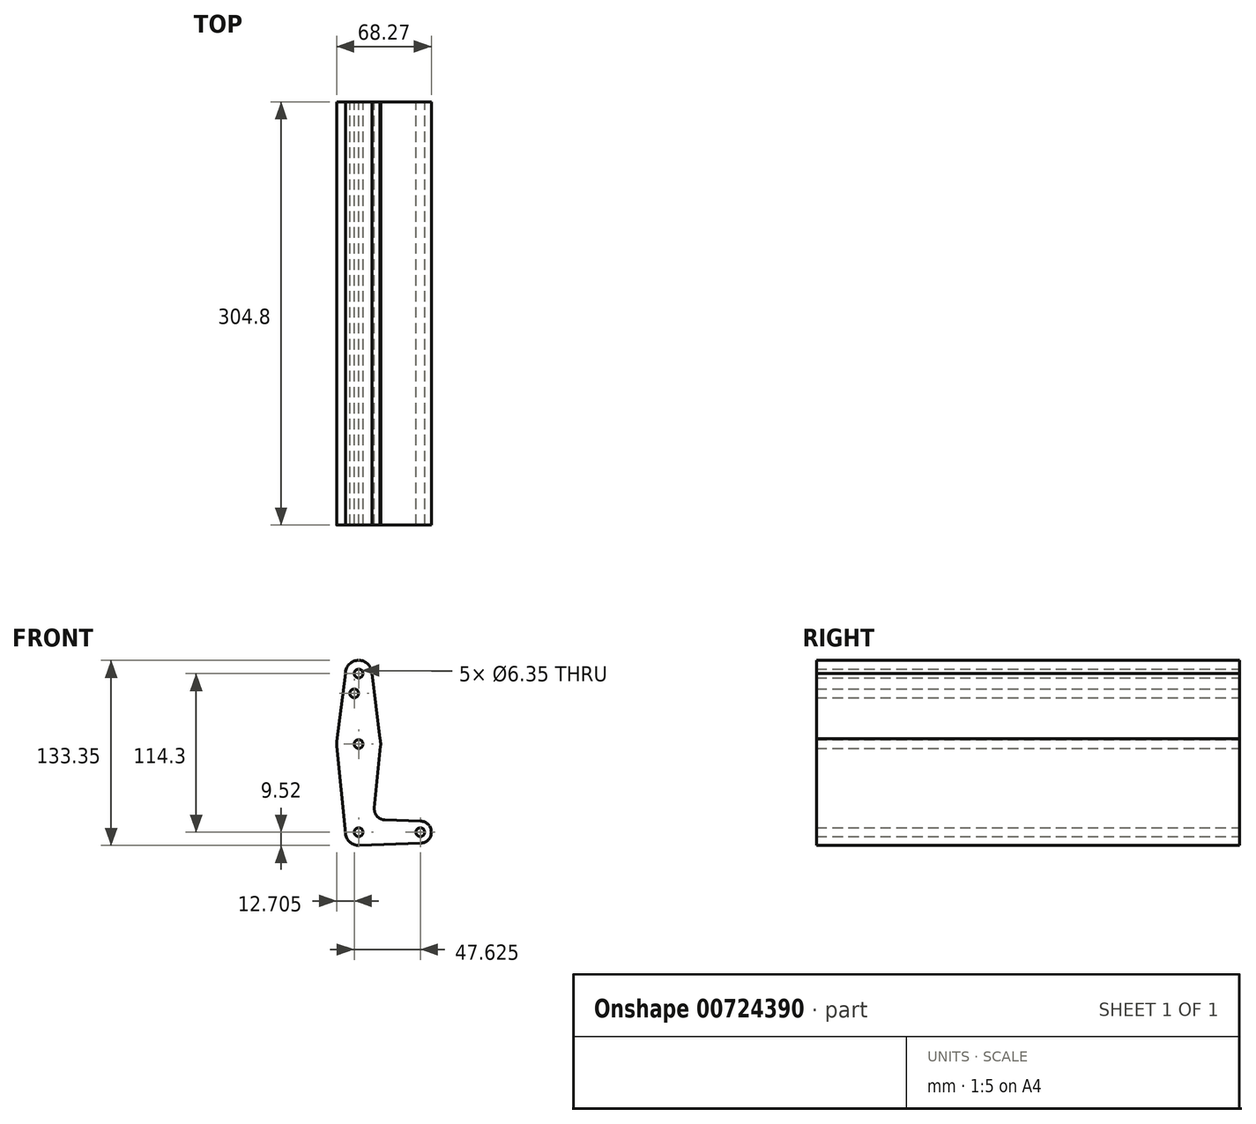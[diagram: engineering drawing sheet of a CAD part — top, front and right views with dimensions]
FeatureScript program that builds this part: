
annotation { "Feature Type Name" : "Feature", "Feature Type Description" : "" }
export const myFeature = defineFeature(function(context is Context, id is Id, definition is map)
    precondition{}
    {
        {
            var Q0;
            Q0=qCreatedBy(makeId("Front.planeOp"),FACE);
            var sketch = newSketch(context, id + "F0", { "sketchPlane" : qUnion([Q0])});
            skLineSegment(sketch, "E0", {"start": v(0, 0) * mm, "end": v(0, 114.3) * mm, "construction": true});
            skLineSegment(sketch, "E1", {"start": v(44.45, 0) * mm, "end": v(0, 0) * mm, "construction": true});
            skCircle(sketch, "E2", {"center": v(0, 114.3) * mm, "radius": 9.53 * mm});
            skCircle(sketch, "E3", {"center": v(0, 63.5) * mm, "radius": 15.88 * mm});
            skCircle(sketch, "E4", {"center": v(0, 0) * mm, "radius": 9.53 * mm});
            skCircle(sketch, "E5", {"center": v(44.45, 0) * mm, "radius": 7.94 * mm});
            skLineSegment(sketch, "E6", {"start": v(-9.53, 114.3) * mm, "end": v(-16, 63.5) * mm});
            skLineSegment(sketch, "E7", {"start": v(9.52, 114.3) * mm, "end": v(15.88, 63.5) * mm});
            skCircle(sketch, "E8", {"center": v(0, 114.3) * mm, "radius": 3.18 * mm});
            skCircle(sketch, "E9", {"center": v(0, 63.5) * mm, "radius": 3.18 * mm});
            skCircle(sketch, "E10", {"center": v(0, 0) * mm, "radius": 3.18 * mm});
            skCircle(sketch, "E11", {"center": v(44.45, 0) * mm, "radius": 3.18 * mm});
            skCircle(sketch, "E12", {"center": v(-3.18, 100.03) * mm, "radius": 3.18 * mm});
            skLineSegment(sketch, "E13", {"start": v(-15.8, 61.91) * mm, "end": v(-9.48, -0.95) * mm});
            skLineSegment(sketch, "E14", {"start": v(15.8, 61.91) * mm, "end": v(11.34, 17.6) * mm});
            skLineSegment(sketch, "E15", {"start": v(18.97, 8.85) * mm, "end": v(44.73, 7.93) * mm});
            skLineSegment(sketch, "E16", {"start": v(0.34, -9.52) * mm, "end": v(44.73, -7.93) * mm});
            skArc(sketch, "E17.filletArc", {"start": v(11.34, 17.6) * mm, "mid": v(13.26, 11.57) * mm, "end": v(18.97, 8.85) * mm});
            skSolve(sketch);
        }
        {
            var Q0;
            Q0 = qSketchRegion(id + "F0", true);
            extrude(context, id + "F1", {"entities" : qUnion([Q0]), "depth" : 304.8 * mm, "offsetDistance" : 25.4 * mm});
        }
    });
